# Revit family: Bath-Alcove-Kohler-Hourglass-K_1219
name_source: partatom
category: Plumbing Fixtures
revit_build: Autodesk Revit 2015 (Build: 20140606_1530(x64)
units: mm (PartAtom-declared; Revit-internal decimal feet)

## types (6) — shared parameters
ADA Compliant = No
Assembly Code = D2010510
CW Connection = No
Default Elevation = 0' - 0"
Drain Diameter = 0' - 1 1/2"
HW Connection = No
Height = 1' - 9 1/4"
Length = 5' - 0"
Manufacturer = Kohler
Material = Acrylic
Product Documentation Link = http://www.us.kohler.com
Product Name = Hourglass 60'' x 32'' Alcove Bath with Flange
Product Page URL = http://www.us.kohler.com
Sanitary Connector = Sanitary Drain
URL = http://www.us.kohler.com
Vent Connection = Yes
Version = 2014 - v1.0a
Waste Connection = Yes
Water Capacity = 64 gal (234.4 L)
Weight = 80 lbs (36.3 kg)
Width = 2' - 8"
zero-valued in all types: CWFU, HWFU, WFU

## per-type parameters (varying)
| type | Constraint | ControlM | Description | Finish | Keynote | Model |
| Right Drain, 0-White | 1 | 0 | 60'' x 32'' Alcove Bath, Right Hand Drain with Flange, White | Acrylic - Kohler - 0 - White | 22 40 00.D2 | K-1219-R-0 |
| Right Drain, 47-Almond | 1 | 47 | 60'' x 32'' Alcove Bath, Right Hand Drain with Flange, Almond | Acrylic - Kohler - 47 - Almond | 22 40 00.D2 | K-1219-R-47 |
| Right Drain, 96-Biscuit | 1 | 96 | 60'' x 32'' Alcove Bath, Right Hand Drain with Flange, Biscuit | Acrylic - Kohler - 96 - Biscuit | 22 40 00.D4 | K-1219-R-96 |
| Left Drain, 0-White | 2 | 0 | 60'' x 32'' Alcove Bath, Left Hand Drain with Flange, White | Acrylic - Kohler - 0 - White | 22 40 00.D2 | K-1219-L-0 |
| Left Drain, 47-Almond | 2 | 47 | 60'' x 32'' Alcove Bath, Left Hand Drain with Flange, Almond | Acrylic - Kohler - 47 - Almond | 22 40 00.D2 | K-1219-L-47 |
| Left Drain, 96-Biscuit | 2 | 96 | 60'' x 32'' Alcove Bath, Left Hand Drain with Flange, Biscuit | Acrylic - Kohler - 96 - Biscuit | 22 40 00.D2 | K-1219-L-96 |

## geometry (parser evidence)
native form markers: Sweep x6
no freeform markers — native parametric forms only
